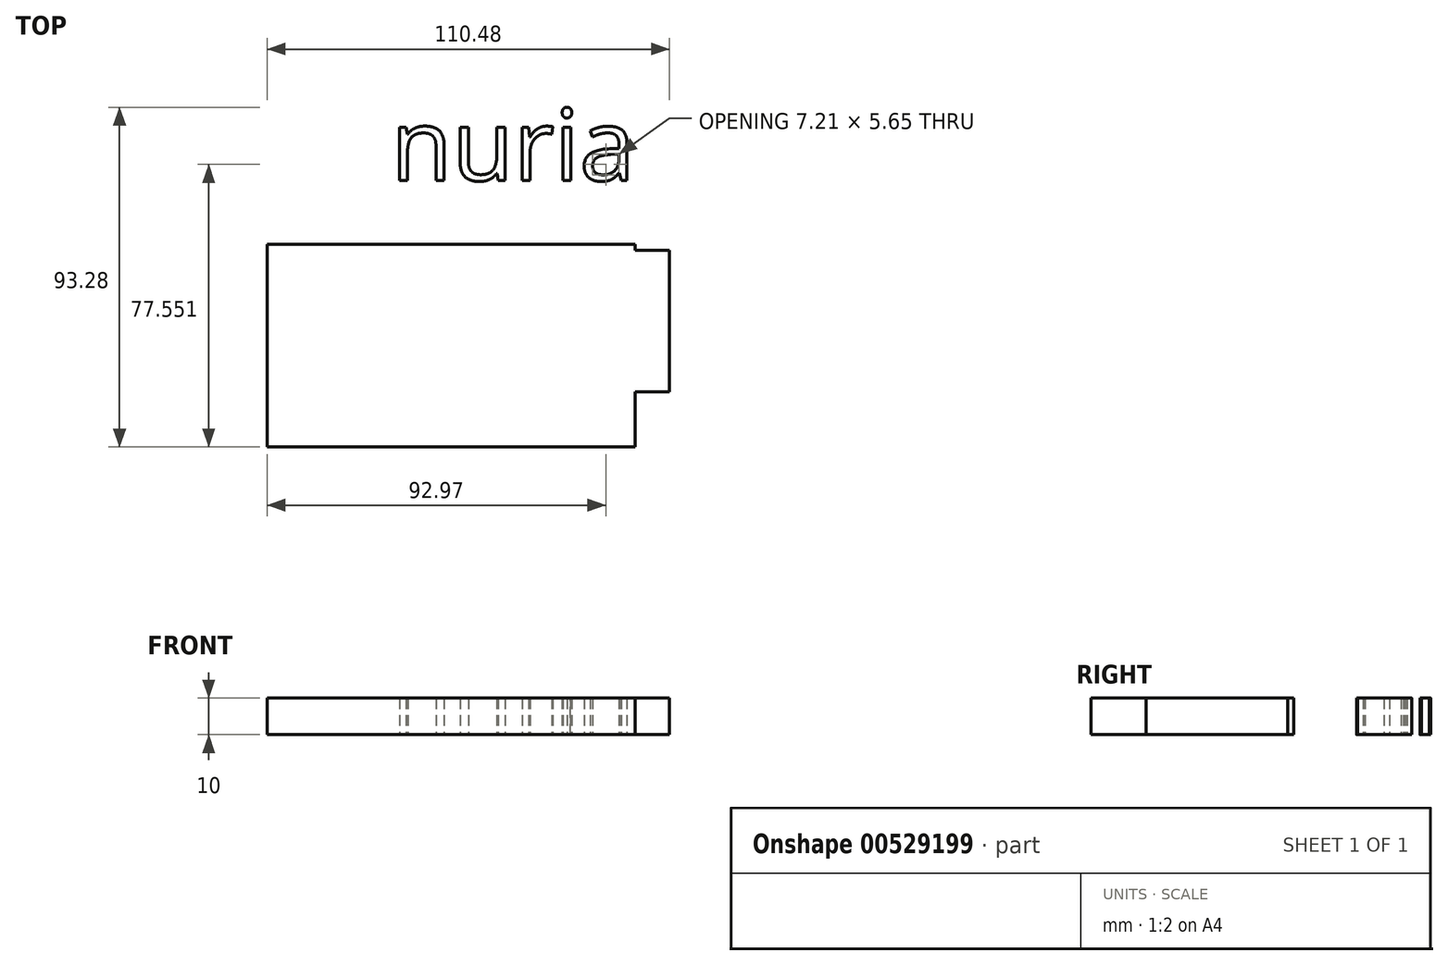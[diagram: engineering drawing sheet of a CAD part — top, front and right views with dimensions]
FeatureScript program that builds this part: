
annotation { "Feature Type Name" : "Feature", "Feature Type Description" : "" }
export const myFeature = defineFeature(function(context is Context, id is Id, definition is map)
    precondition{}
    {
        {
            var Q0;
            Q0=qCreatedBy(makeId("Top.planeOp"),FACE);
            var sketch = newSketch(context, id + "F0", { "sketchPlane" : qUnion([Q0])});
            skLineSegment(sketch, "E0.bottom", {"start": v(-38.26, 18.77) * mm, "end": v(34.16, 18.77) * mm});
            skLineSegment(sketch, "E0.top", {"start": v(-38.26, -20.06) * mm, "end": v(34.16, -20.06) * mm});
            skLineSegment(sketch, "E0.left", {"start": v(-38.26, 18.77) * mm, "end": v(-38.26, -20.06) * mm});
            skLineSegment(sketch, "E0.right", {"start": v(34.16, 18.77) * mm, "end": v(34.16, -20.06) * mm});
            skLineSegment(sketch, "E1.bottom", {"start": v(-76.32, 20.45) * mm, "end": v(24.64, 20.45) * mm});
            skLineSegment(sketch, "E1.top", {"start": v(-76.32, -35.23) * mm, "end": v(24.64, -35.23) * mm});
            skLineSegment(sketch, "E1.left", {"start": v(-76.32, 20.45) * mm, "end": v(-76.32, -35.23) * mm});
            skLineSegment(sketch, "E1.right", {"start": v(24.64, 20.45) * mm, "end": v(24.64, -35.23) * mm});
            skText(sketch, "E2", { "text": "nuria\n", "fontName": "OpenSans-Regular.ttf"});
            const initialGuessF0  = {"E2": [-0.04233, 0.03793, 1, 0, 0.01974]};
            skSetInitialGuess(sketch, initialGuessF0);
            skSolve(sketch);
        }
        {
            var Q0;
            Q0 = qSketchRegion(id + "F0", true);
            extrude(context, id + "F1", {"entities" : qUnion([Q0]), "depth" : 10 * mm, "offsetDistance" : 25 * mm});
        }
    });
